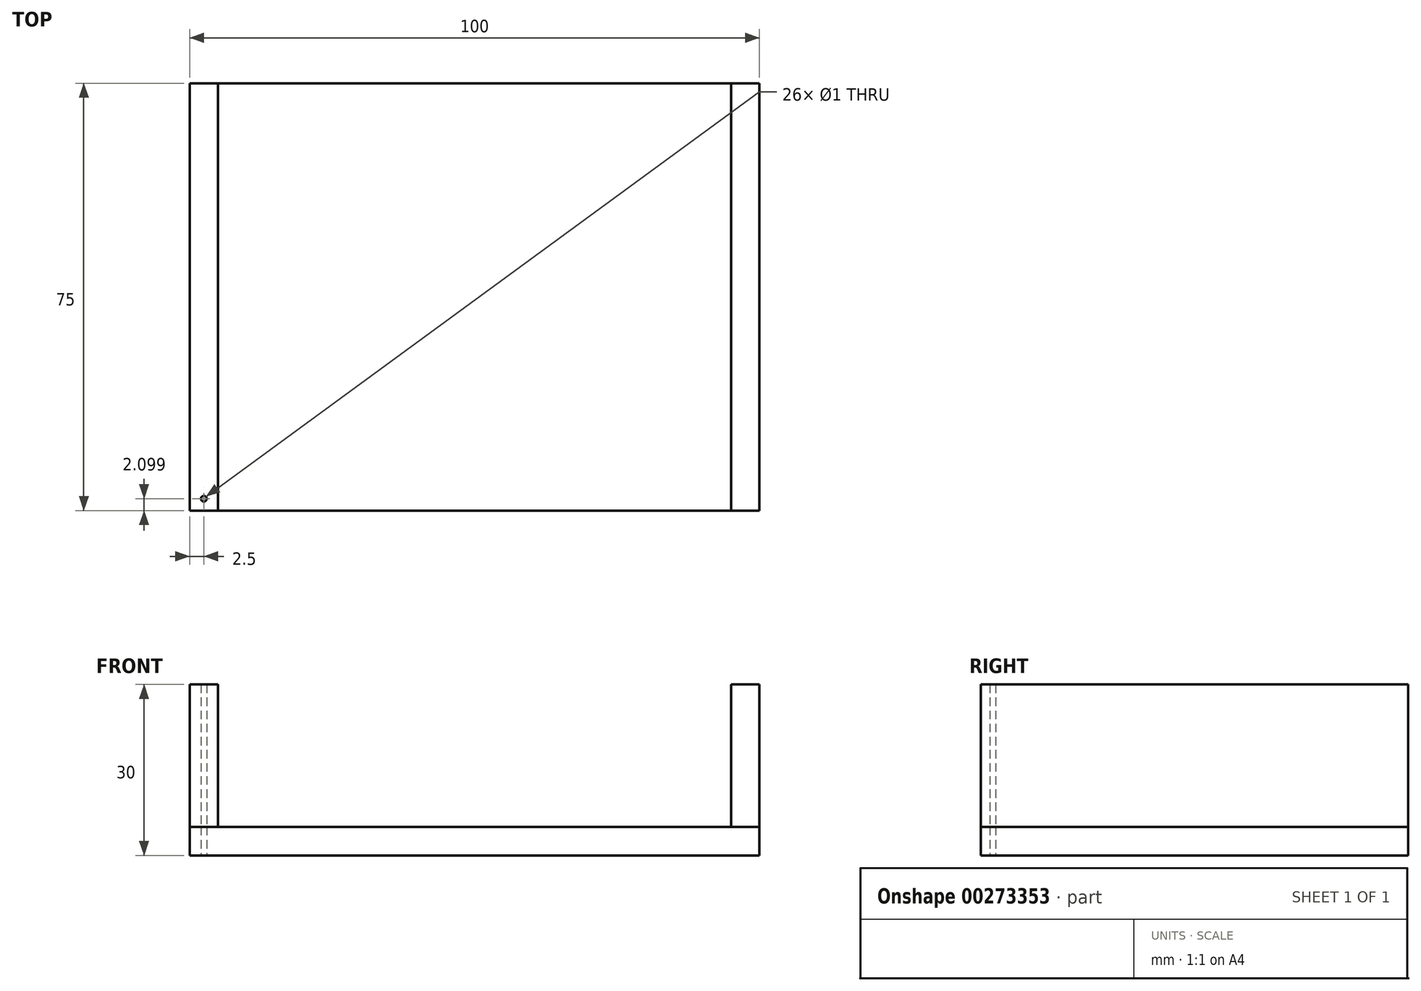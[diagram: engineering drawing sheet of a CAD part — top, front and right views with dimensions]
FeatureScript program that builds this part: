
annotation { "Feature Type Name" : "Feature", "Feature Type Description" : "" }
export const myFeature = defineFeature(function(context is Context, id is Id, definition is map)
    precondition{}
    {
        {
            var Q0;
            Q0=qCreatedBy(makeId("Top.planeOp"),FACE);
            var sketch = newSketch(context, id + "F0", { "sketchPlane" : qUnion([Q0])});
            skLineSegment(sketch, "E0.bottom", {"start": v(50, 37.5) * mm, "end": v(-50, 37.5) * mm});
            skLineSegment(sketch, "E0.top", {"start": v(50, -37.5) * mm, "end": v(-50, -37.5) * mm});
            skLineSegment(sketch, "E0.left", {"start": v(50, 37.5) * mm, "end": v(50, -37.5) * mm});
            skLineSegment(sketch, "E0.right", {"start": v(-50, 37.5) * mm, "end": v(-50, -37.5) * mm});
            skPoint(sketch, "E0.middle", {"position": v(0, 0) * mm});
            skSolve(sketch);
        }
        {
            var Q0;
            Q0 = qSketchRegion(id + "F0", true);
            extrude(context, id + "F1", {"entities" : qUnion([Q0]), "depth" : 5 * mm});
        }
        {
            var Q0;
            Q0=makeQuery(id+"F1.opExtrude","CAP_FACE",FACE,{"disambiguationData":[OSD([sQuery(id+"F0.wireOp",EDGE,"E0.bottom"),sQuery(id+"F0.wireOp",EDGE,"E0.top"),sQuery(id+"F0.wireOp",EDGE,"E0.left"),sQuery(id+"F0.wireOp",EDGE,"E0.right")])],"isStart":false});
            var sketch = newSketch(context, id + "F2", { "sketchPlane" : qUnion([Q0])});
            skPoint(sketch, "E1.0", {"position": v(-50, 37.5) * mm});
            skLineSegment(sketch, "E2.0", {"start": v(-50, 37.5) * mm, "end": v(-50, -37.5) * mm, "construction": true});
            skLineSegment(sketch, "E3.bottom", {"start": v(-50, 37.5) * mm, "end": v(-45, 37.5) * mm});
            skLineSegment(sketch, "E3.top", {"start": v(-50, -37.5) * mm, "end": v(-45, -37.5) * mm});
            skLineSegment(sketch, "E3.left", {"start": v(-50, 37.5) * mm, "end": v(-50, -37.5) * mm});
            skLineSegment(sketch, "E3.right", {"start": v(-45, 37.5) * mm, "end": v(-45, -37.5) * mm});
            skLineSegment(sketch, "E4", {"start": v(0, 37.5) * mm, "end": v(0, -37.5) * mm, "construction": true});
            skLineSegment(sketch, "E5.MirrorCS", {"start": v(50, 37.5) * mm, "end": v(45, 37.5) * mm});
            skLineSegment(sketch, "E6.MirrorCS", {"start": v(50, 37.5) * mm, "end": v(50, -37.5) * mm});
            skLineSegment(sketch, "E7.MirrorCS", {"start": v(45, 37.5) * mm, "end": v(45, -37.5) * mm});
            skPoint(sketch, "E8.MirrorP", {"position": v(50, 37.5) * mm});
            skLineSegment(sketch, "E9.MirrorCS", {"start": v(50, 37.5) * mm, "end": v(50, -37.5) * mm, "construction": true});
            skLineSegment(sketch, "E10.MirrorCS", {"start": v(50, -37.5) * mm, "end": v(45, -37.5) * mm});
            skSolve(sketch);
        }
        {
            var Q0;
            Q0 = qSketchRegion(id + "F2", true);
            extrude(context, id + "F3", {"entities" : qUnion([Q0]), "depth" : 25 * mm});
        }
        {
            var Q0;
            Q0=makeQuery(id+"F1.opExtrude","CAP_FACE",FACE,{"disambiguationData":[OSD([sQuery(id+"F0.wireOp",EDGE,"E0.bottom"),sQuery(id+"F0.wireOp",EDGE,"E0.top"),sQuery(id+"F0.wireOp",EDGE,"E0.left"),sQuery(id+"F0.wireOp",EDGE,"E0.right")])],"isStart":true});
            var sketch = newSketch(context, id + "F4", { "sketchPlane" : qUnion([Q0])});
            skCircle(sketch, "E11", {"center": v(-47.5, 35.4) * mm, "radius": 0.5 * mm});
            skPoint(sketch, "E12.0", {"position": v(-47.5, 37.5) * mm});
            skLineSegment(sketch, "E13", {"start": v(-47.5, 37.5) * mm, "end": v(-47.5, 1.3) * mm});
            skSolve(sketch);
        }
        {
            var Q0;
            Q0 = qSketchRegion(id + "F4", true);
            extrude(context, id + "F5", {"entities" : qUnion([Q0]), "operationType" : NewBodyOperationType.REMOVE, "oppositeDirection" : true, "depth" : 100 * mm, "hasSecondDirection" : true, "secondDirectionOppositeDirection" : false, "secondDirectionDepth" : 25 * mm});
        }
    });
